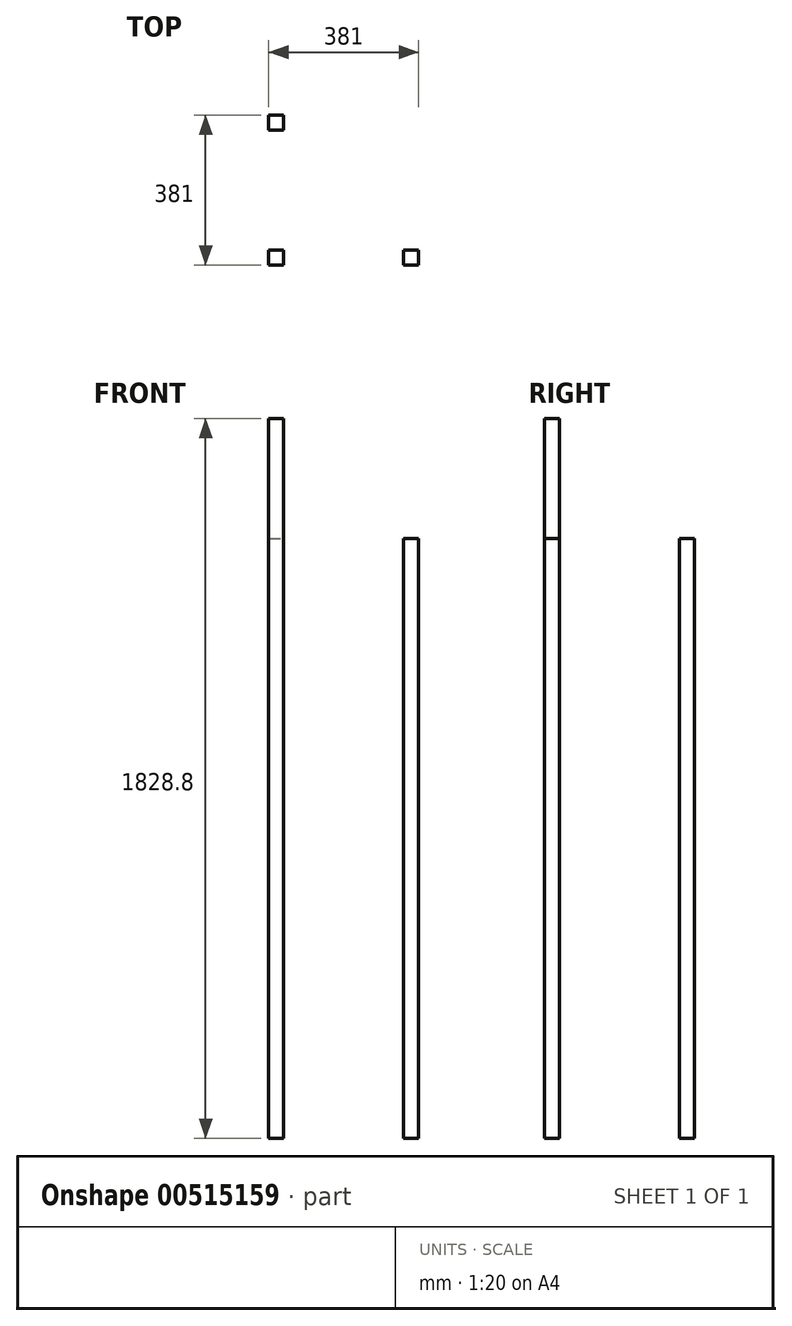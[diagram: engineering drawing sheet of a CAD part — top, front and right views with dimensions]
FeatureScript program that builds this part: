
annotation { "Feature Type Name" : "Feature", "Feature Type Description" : "" }
export const myFeature = defineFeature(function(context is Context, id is Id, definition is map)
    precondition{}
    {
        {
            var Q0;
            Q0=qCreatedBy(makeId("Top.planeOp"),FACE);
            var sketch = newSketch(context, id + "F0", { "sketchPlane" : qUnion([Q0])});
            skLineSegment(sketch, "E0.bottom", {"start": v(0, 0) * mm, "end": v(38.1, 0) * mm});
            skLineSegment(sketch, "E0.top", {"start": v(0, 38.1) * mm, "end": v(38.1, 38.1) * mm});
            skLineSegment(sketch, "E0.left", {"start": v(0, 0) * mm, "end": v(0, 38.1) * mm});
            skLineSegment(sketch, "E0.right", {"start": v(38.1, 0) * mm, "end": v(38.1, 38.1) * mm});
            skLineSegment(sketch, "E1.bottom", {"start": v(0, 342.9) * mm, "end": v(38.1, 342.9) * mm});
            skLineSegment(sketch, "E1.top", {"start": v(0, 381) * mm, "end": v(38.1, 381) * mm});
            skLineSegment(sketch, "E1.left", {"start": v(0, 342.9) * mm, "end": v(0, 381) * mm});
            skLineSegment(sketch, "E1.right", {"start": v(38.1, 342.9) * mm, "end": v(38.1, 381) * mm});
            skPoint(sketch, "E2.firstSnap0", {"position": v(19.05, 0) * mm});
            skLineSegment(sketch, "E2.bottom", {"start": v(342.9, 0) * mm, "end": v(381, 0) * mm});
            skLineSegment(sketch, "E2.top", {"start": v(342.9, 38.1) * mm, "end": v(381, 38.1) * mm});
            skLineSegment(sketch, "E2.left", {"start": v(342.9, 0) * mm, "end": v(342.9, 38.1) * mm});
            skLineSegment(sketch, "E2.right", {"start": v(381, 0) * mm, "end": v(381, 38.1) * mm});
            skSolve(sketch);
        }
        {
            var Q0;
            Q0=makeQuery(id+"F0.imprint","IMPRINT",FACE,{"disambiguationData":[TD([[makeQuery(id+"F0.imprint","IMPRINT",EDGE,{"derivedFrom":sQuery(id+"F0.wireOp",EDGE,"E0.bottom")}),1.0]])]});
            extrude(context, id + "F1", {"entities" : qUnion([Q0]), "depth" : 1828.8 * mm, "offsetDistance" : 25.4 * mm});
        }
        {
            var Q0;
            Q0=makeQuery(id+"F0.imprint","IMPRINT",FACE,{"disambiguationData":[TD([[makeQuery(id+"F0.imprint","IMPRINT",EDGE,{"derivedFrom":sQuery(id+"F0.wireOp",EDGE,"E1.bottom")}),1.0]])]});
            var Q1;
            Q1=makeQuery(id+"F0.imprint","IMPRINT",FACE,{"disambiguationData":[TD([[makeQuery(id+"F0.imprint","IMPRINT",EDGE,{"derivedFrom":sQuery(id+"F0.wireOp",EDGE,"E2.bottom")}),1.0]])]});
            extrude(context, id + "F2", {"entities" : qUnion([Q0, Q1]), "depth" : 1524 * mm, "offsetDistance" : 25.4 * mm});
        }
    });
